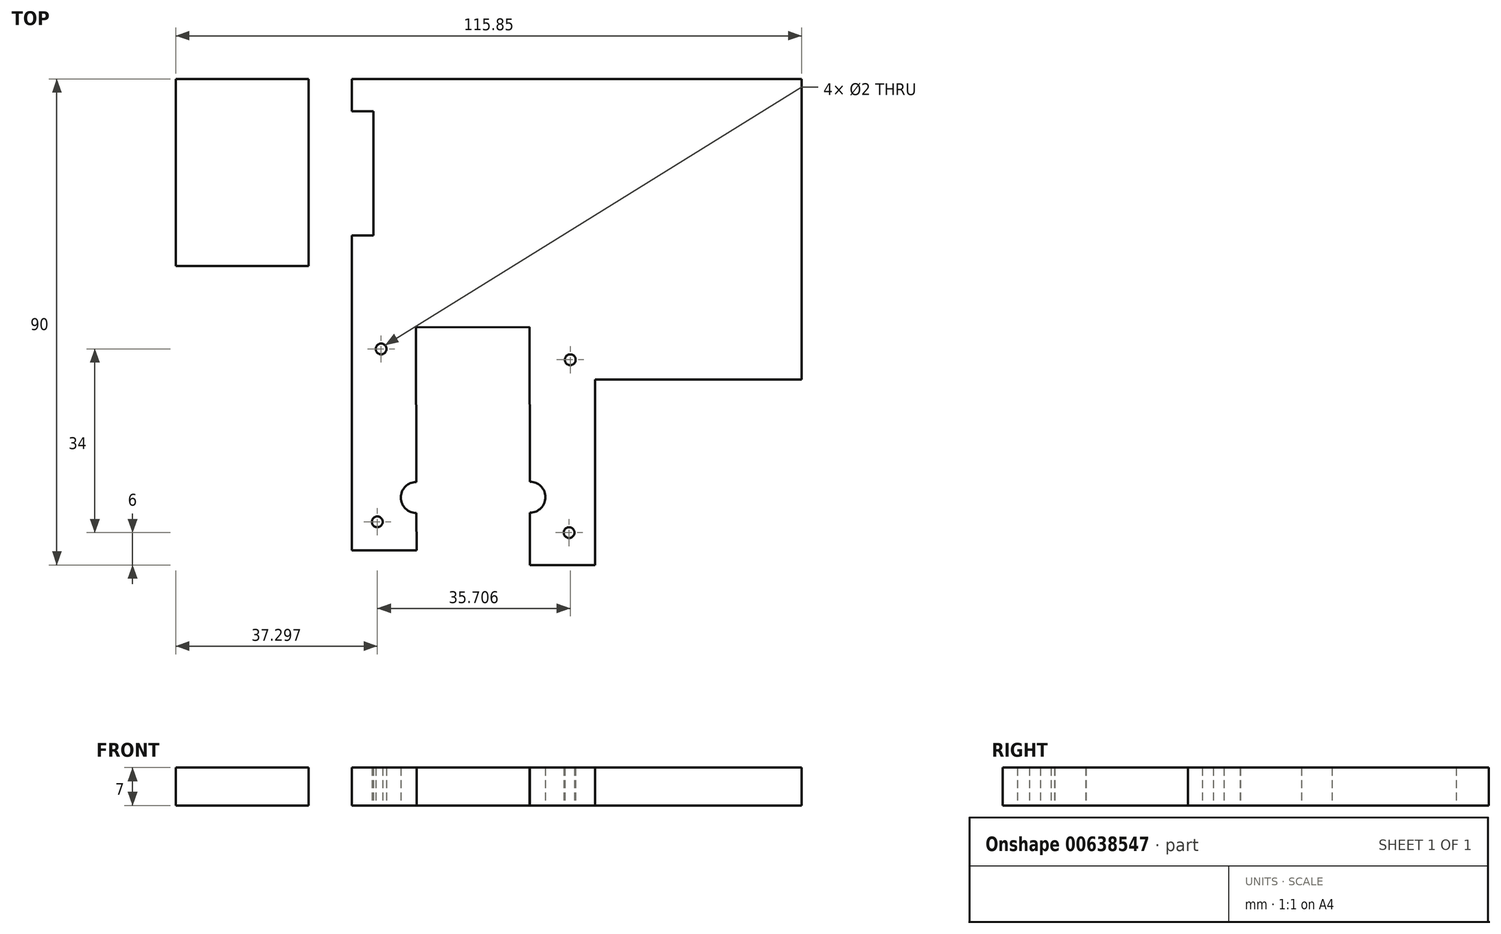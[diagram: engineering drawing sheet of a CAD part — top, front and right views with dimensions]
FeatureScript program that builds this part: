
annotation { "Feature Type Name" : "Feature", "Feature Type Description" : "" }
export const myFeature = defineFeature(function(context is Context, id is Id, definition is map)
    precondition{}
    {
        {
            var Q0;
            Q0=qCreatedBy(makeId("Top.planeOp"),FACE);
            var sketch = newSketch(context, id + "F0", { "sketchPlane" : qUnion([Q0])});
            skLineSegment(sketch, "E0.bottom", {"start": v(22.5, -45) * mm, "end": v(10.5, -45) * mm});
            skLineSegment(sketch, "E0.top", {"start": v(22.5, 45) * mm, "end": v(-22.5, 45) * mm});
            skLineSegment(sketch, "E0.left", {"start": v(22.5, -45) * mm, "end": v(22.5, 45) * mm});
            skLineSegment(sketch, "E0.right", {"start": v(-22.5, -42.25) * mm, "end": v(-22.5, 45) * mm});
            skPoint(sketch, "E0.middle", {"position": v(0, 0) * mm});
            skLineSegment(sketch, "E1.bottom", {"start": v(-10.63, -1) * mm, "end": v(10.37, -0.94) * mm});
            skLineSegment(sketch, "E1.left", {"start": v(-10.63, -1) * mm, "end": v(-10.5, -42.25) * mm});
            skLineSegment(sketch, "E1.right", {"start": v(10.37, -0.94) * mm, "end": v(10.5, -45) * mm});
            skLineSegment(sketch, "E2.bottom", {"start": v(-22.5, 39) * mm, "end": v(-14.5, 39) * mm});
            skLineSegment(sketch, "E2.top", {"start": v(-22.5, 45) * mm, "end": v(-14.5, 45) * mm});
            skLineSegment(sketch, "E2.left", {"start": v(-22.5, 39) * mm, "end": v(-22.5, 45) * mm});
            skLineSegment(sketch, "E2.right", {"start": v(-14.5, 39) * mm, "end": v(-14.5, 45) * mm});
            skLineSegment(sketch, "E3.bottom", {"start": v(-22.5, 16) * mm, "end": v(-14.5, 16) * mm});
            skLineSegment(sketch, "E3.top", {"start": v(-22.5, 10.36) * mm, "end": v(-14.5, 10.36) * mm});
            skLineSegment(sketch, "E3.left", {"start": v(-22.5, 16) * mm, "end": v(-22.5, 10.36) * mm});
            skLineSegment(sketch, "E3.right", {"start": v(-14.5, 16) * mm, "end": v(-14.5, 10.36) * mm});
            skPoint(sketch, "E4", {"position": v(-17.77, -37) * mm});
            skPoint(sketch, "E5", {"position": v(-17.07, -5) * mm});
            skPoint(sketch, "E6", {"position": v(17.93, -7) * mm});
            skPoint(sketch, "E7", {"position": v(17.73, -39) * mm});
            skPoint(sketch, "E8.positionSnap0", {"position": v(-18.5, 45) * mm});
            skPoint(sketch, "E9.positionSnap0", {"position": v(-18.5, 16) * mm});
            skPoint(sketch, "E10", {"position": v(-10.54, -32.5) * mm});
            skPoint(sketch, "E11", {"position": v(0, 45) * mm});
            skPoint(sketch, "E12", {"position": v(22.5, 17.15) * mm});
            skLineSegment(sketch, "E13", {"start": v(0, 45) * mm, "end": v(22.5, 17.15) * mm});
            skPoint(sketch, "E14", {"position": v(10.46, -32.44) * mm});
            skLineSegment(sketch, "E15", {"start": v(0, -64.42) * mm, "end": v(0, 71.46) * mm, "construction": true});
            skPoint(sketch, "E16", {"position": v(-22.5, -39) * mm});
            skPoint(sketch, "E17", {"position": v(-22.5, -42.25) * mm});
            skLineSegment(sketch, "E18", {"start": v(-22.5, -42.25) * mm, "end": v(-10.5, -42.25) * mm});
            skPoint(sketch, "E19.trimOffspring.end.orphan", {"position": v(-22.5, -45) * mm});
            skLineSegment(sketch, "E20.MirrorCS", {"start": v(-30.5, 16) * mm, "end": v(-30.5, 10.36) * mm});
            skLineSegment(sketch, "E21.MirrorCS", {"start": v(-22.5, 10.36) * mm, "end": v(-30.5, 10.36) * mm});
            skLineSegment(sketch, "E22", {"start": v(-22.5, 16) * mm, "end": v(-30.5, 16) * mm});
            skLineSegment(sketch, "E23.MirrorCS", {"start": v(-22.5, 39) * mm, "end": v(-30.5, 39) * mm});
            skLineSegment(sketch, "E24.MirrorCS", {"start": v(-30.5, 39) * mm, "end": v(-30.5, 45) * mm});
            skLineSegment(sketch, "E25", {"start": v(-22.5, 45) * mm, "end": v(-30.5, 45) * mm});
            skLineSegment(sketch, "E26", {"start": v(-14.5, 39) * mm, "end": v(-14.5, 16) * mm});
            skLineSegment(sketch, "E27", {"start": v(-30.5, 39) * mm, "end": v(-30.5, 16) * mm});
            skLineSegment(sketch, "E28", {"start": v(-30.5, 10.36) * mm, "end": v(-55.07, 10.36) * mm});
            skLineSegment(sketch, "E29", {"start": v(-55.07, 10.36) * mm, "end": v(-55.07, 45) * mm});
            skLineSegment(sketch, "E30", {"start": v(-55.07, 45) * mm, "end": v(-30.5, 45) * mm});
            skLineSegment(sketch, "E31", {"start": v(22.5, 45) * mm, "end": v(60.78, 45) * mm});
            skLineSegment(sketch, "E32", {"start": v(60.78, 45) * mm, "end": v(60.78, -10.65) * mm});
            skLineSegment(sketch, "E33", {"start": v(60.78, -10.65) * mm, "end": v(22.5, -10.65) * mm});
            skLineSegment(sketch, "E34", {"start": v(-55.07, 45) * mm, "end": v(-55.07, 56.77) * mm});
            skLineSegment(sketch, "E35", {"start": v(-55.07, 56.77) * mm, "end": v(60.64, 56.77) * mm});
            skLineSegment(sketch, "E36", {"start": v(60.64, 56.77) * mm, "end": v(60.78, 45) * mm});
            skPoint(sketch, "E37", {"position": v(-18.5, 39) * mm});
            skLineSegment(sketch, "E38", {"start": v(-18.5, 39) * mm, "end": v(-18.5, 16) * mm});
            skSolve(sketch);
        }
        {
            var Q0;
            Q0=makeQuery(id+"F0.imprint","IMPRINT",FACE,{"disambiguationData":[TD([[makeQuery(id+"F0.imprint","IMPRINT",EDGE,{"derivedFrom":sQuery(id+"F0.wireOp",EDGE,"E0.bottom")}),-1.0]])]});
            var Q1;
            {var subQ3=sQuery(id+"F0.wireOp",EDGE,"E13");Q1=makeQuery(id+"F0.imprint","IMPRINT",FACE,{"disambiguationData":[TD([[makeQuery(id+"F0.imprint","IMPRINT",EDGE,{"derivedFrom":subQ3}),1.0]])]});}
            var Q2;
            Q2=makeQuery(id+"F0.imprint","IMPRINT",FACE,{"disambiguationData":[TD([[makeQuery(id+"F0.imprint","IMPRINT",EDGE,{"derivedFrom":sQuery(id+"F0.wireOp",EDGE,"E20.MirrorCS")}),-1.0]])]});
            var Q3;
            Q3=makeQuery(id+"F0.imprint","IMPRINT",FACE,{"disambiguationData":[TD([[makeQuery(id+"F0.imprint","IMPRINT",EDGE,{"derivedFrom":sQuery(id+"F0.wireOp",EDGE,"E2.left")}),1.0]])]});
            var Q4;
            Q4=makeQuery(id+"F0.imprint","IMPRINT",FACE,{"disambiguationData":[TD([[makeQuery(id+"F0.imprint","IMPRINT",EDGE,{"derivedFrom":sQuery(id+"F0.wireOp",EDGE,"E2.bottom")}),1.0]])]});
            var Q5;
            Q5=makeQuery(id+"F0.imprint","IMPRINT",FACE,{"disambiguationData":[TD([[makeQuery(id+"F0.imprint","IMPRINT",EDGE,{"derivedFrom":sQuery(id+"F0.wireOp",EDGE,"E3.bottom")}),-1.0]])]});
            var Q6;
            Q6=makeQuery(id+"F0.imprint","IMPRINT",FACE,{"disambiguationData":[TD([[makeQuery(id+"F0.imprint","IMPRINT",EDGE,{"derivedFrom":sQuery(id+"F0.wireOp",EDGE,"E3.left")}),-1.0]])]});
            var Q7;
            {var subQ0=sQuery(id+"F0.wireOp",EDGE,"E31");Q7=makeQuery(id+"F0.imprint","IMPRINT",FACE,{"disambiguationData":[TD([[makeQuery(id+"F0.imprint","IMPRINT",EDGE,{"derivedFrom":subQ0}),-1.0]])]});}
            var Q8;
            {var subQ0=sQuery(id+"F0.wireOp",EDGE,"E2.top");Q8=makeQuery(id+"F0.imprint","IMPRINT",FACE,{"disambiguationData":[TD([[makeQuery(id+"F0.imprint","IMPRINT",EDGE,{"derivedFrom":subQ0}),1.0]])]});}
            var Q9;
            {var subQ0=sQuery(id+"F0.wireOp",EDGE,"E26");Q9=makeQuery(id+"F0.imprint","IMPRINT",FACE,{"disambiguationData":[TD([[makeQuery(id+"F0.imprint","IMPRINT",EDGE,{"derivedFrom":subQ0}),-1.0]])]});}
            extrude(context, id + "F1", {"entities" : qUnion([Q0, Q1, Q2, Q3, Q4, Q5, Q6, Q7, Q8, Q9]), "depth" : 7 * mm, "offsetDistance" : 25 * mm});
        }
        {
            var Q0;
            Q0=sQuery(id+"F0.wireOp",VERTEX,"E5");
            var Q1;
            Q1=sQuery(id+"F0.wireOp",VERTEX,"E4");
            var Q2;
            Q2=sQuery(id+"F0.wireOp",VERTEX,"E7");
            var Q3;
            Q3=sQuery(id+"F0.wireOp",VERTEX,"E6");
            var Q4;
            Q4=makeQuery(id+"F1.opExtrude","SWEPT_BODY",BODY,{"disambiguationData":[OSD([sQuery(id+"F0.wireOp",EDGE,"E0.bottom"),sQuery(id+"F0.wireOp",EDGE,"E0.top"),sQuery(id+"F0.wireOp",EDGE,"E0.left"),sQuery(id+"F0.wireOp",EDGE,"E0.right"),sQuery(id+"F0.wireOp",EDGE,"E1.bottom"),sQuery(id+"F0.wireOp",EDGE,"E1.left"),sQuery(id+"F0.wireOp",EDGE,"E1.right"),sQuery(id+"F0.wireOp",EDGE,"E2.bottom"),sQuery(id+"F0.wireOp",EDGE,"E2.right"),sQuery(id+"F0.wireOp",EDGE,"E3.bottom"),sQuery(id+"F0.wireOp",EDGE,"E3.top"),sQuery(id+"F0.wireOp",EDGE,"E3.right"),sQuery(id+"F0.wireOp",EDGE,"E19.trimOffspring")])]});
            hole(context, id + "F2", {"style" : HoleStyle.SIMPLE, "endStyle" : HoleEndStyle.THROUGH, "oppositeDirection" : true, "holeDiameter" : 2 * mm, "isTappedThrough" : true, "tappedDepth" : 12.7 * mm, "tapClearance" : 3, "locations" : qUnion([Q0, Q1, Q2, Q3]), "scope" : qUnion([Q4])});
        }
        {
            var Q0;
            Q0=sQuery(id+"F0.wireOp",VERTEX,"E10");
            var Q1;
            Q1=sQuery(id+"F0.wireOp",VERTEX,"E14");
            var Q2;
            Q2=makeQuery(id+"F1.opExtrude","SWEPT_BODY",BODY,{"disambiguationData":[OSD([sQuery(id+"F0.wireOp",EDGE,"E0.bottom"),sQuery(id+"F0.wireOp",EDGE,"E0.top"),sQuery(id+"F0.wireOp",EDGE,"E0.left"),sQuery(id+"F0.wireOp",EDGE,"E0.right"),sQuery(id+"F0.wireOp",EDGE,"E1.bottom"),sQuery(id+"F0.wireOp",EDGE,"E1.left"),sQuery(id+"F0.wireOp",EDGE,"E1.right"),sQuery(id+"F0.wireOp",EDGE,"E2.bottom"),sQuery(id+"F0.wireOp",EDGE,"E2.right"),sQuery(id+"F0.wireOp",EDGE,"E3.bottom"),sQuery(id+"F0.wireOp",EDGE,"E3.top"),sQuery(id+"F0.wireOp",EDGE,"E3.right"),sQuery(id+"F0.wireOp",EDGE,"E19.trimOffspring")])]});
            hole(context, id + "F3", {"style" : HoleStyle.SIMPLE, "endStyle" : HoleEndStyle.THROUGH, "oppositeDirection" : true, "holeDiameter" : 5.75 * mm, "isTappedThrough" : true, "tappedDepth" : 12.7 * mm, "tapClearance" : 3, "locations" : qUnion([Q0, Q1]), "scope" : qUnion([Q2])});
        }
    });
